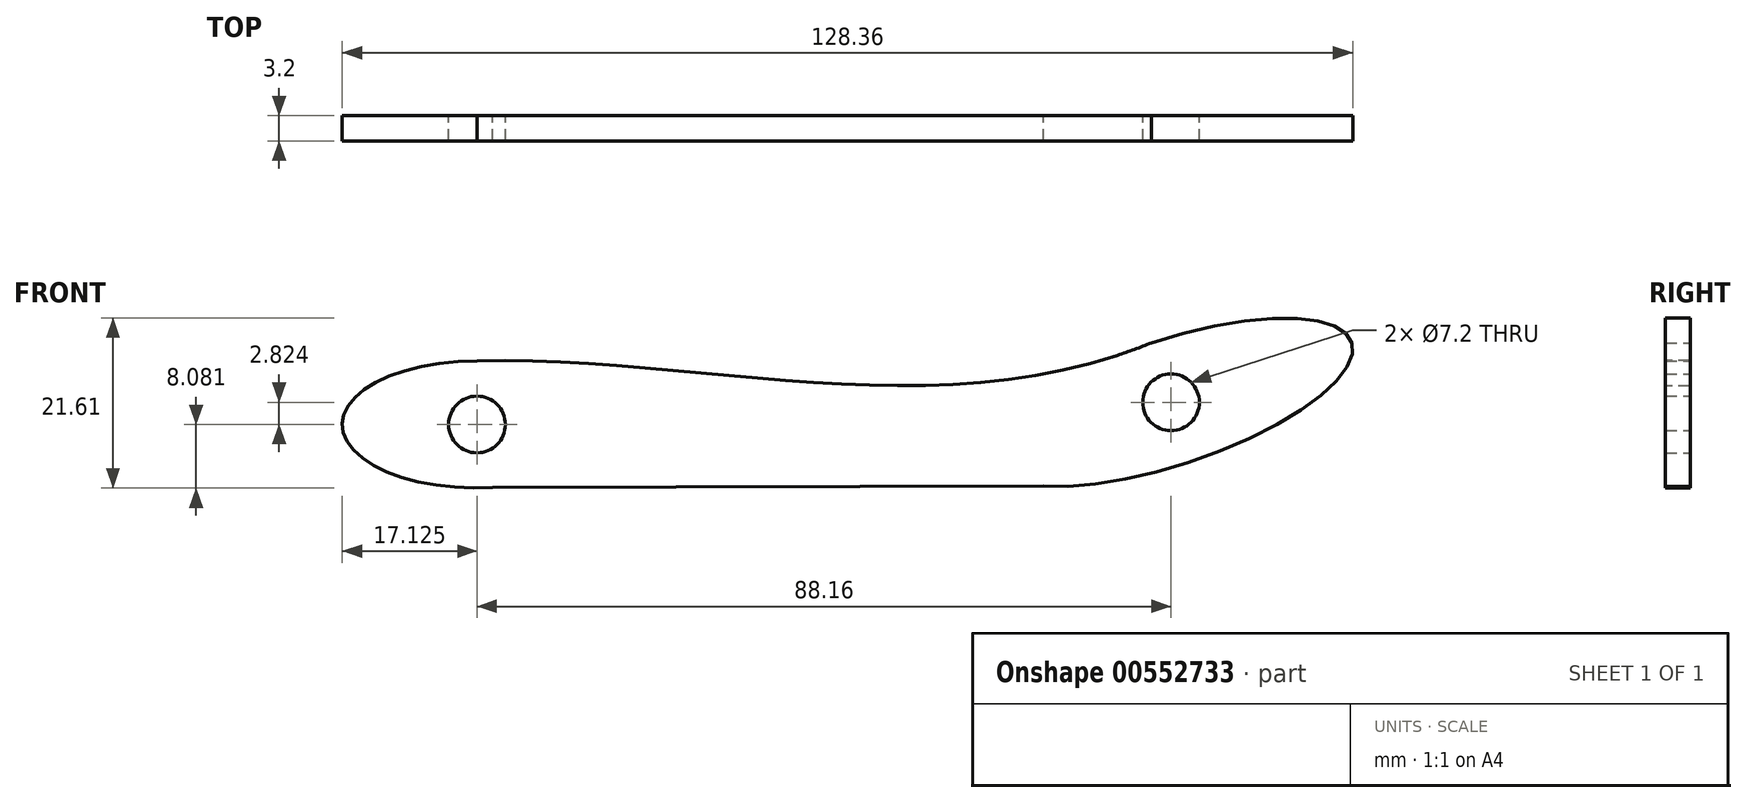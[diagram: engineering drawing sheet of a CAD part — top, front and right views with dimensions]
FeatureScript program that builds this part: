
annotation { "Feature Type Name" : "Feature", "Feature Type Description" : "" }
export const myFeature = defineFeature(function(context is Context, id is Id, definition is map)
    precondition{}
    {
        {
            var Q0;
            Q0=qCreatedBy(makeId("Front.planeOp"),FACE);
            var sketch = newSketch(context, id + "F0", { "sketchPlane" : qUnion([Q0])});
            skEllipse(sketch, "E0", {"center": v(35.66, 0.71) * mm, "majorRadius": 24.16 * mm, "minorRadius": 7.95 * mm, "majorAxis": v(0.95, 0.31)});
            skEllipse(sketch, "E1", {"center": v(-52.5, -2.1) * mm, "majorRadius": 17.12 * mm, "minorRadius": 8.08 * mm, "majorAxis": v(1, 0)});
            skPoint(sketch, "E2.endSnap0", {"position": v(58.6, 8.31) * mm});
            skFitSpline(sketch, "E3", {"points": [v(-52.5, 5.97) * mm, v(33.17, 8.26) * mm], "startDerivative": vector(85.66, 2.27) * mm, "endDerivative": vector(82.56, 33.57) * mm});
            skLineSegment(sketch, "E4", {"start": v(-50.5, -10.13) * mm, "end": v(19.43, -9.94) * mm});
            skCircle(sketch, "E5", {"center": v(35.66, 0.71) * mm, "radius": 3.6 * mm});
            skCircle(sketch, "E6", {"center": v(-52.5, -2.1) * mm, "radius": 3.6 * mm});
            skSolve(sketch);
        }
        {
            var Q0;
            {var subQ0=sQuery(id+"F0.wireOp",EDGE,"E4");Q0=makeQuery(id+"F0.imprint","IMPRINT",FACE,{"disambiguationData":[TD([[makeQuery(id+"F0.imprint","IMPRINT",EDGE,{"derivedFrom":subQ0}),1.0]])]});}
            var Q1;
            Q1=makeQuery(id+"F0.imprint","IMPRINT",FACE,{"disambiguationData":[TD([[makeQuery(id+"F0.imprint","IMPRINT",EDGE,{"derivedFrom":sQuery(id+"F0.wireOp",EDGE,"E6")}),-1.0]])]});
            var Q2;
            Q2=makeQuery(id+"F0.imprint","IMPRINT",FACE,{"disambiguationData":[TD([[makeQuery(id+"F0.imprint","IMPRINT",EDGE,{"derivedFrom":sQuery(id+"F0.wireOp",EDGE,"E5")}),-1.0]])]});
            extrude(context, id + "F1", {"entities" : qUnion([Q0, Q1, Q2]), "depth" : 3.2 * mm, "offsetDistance" : 25 * mm});
        }
    });
